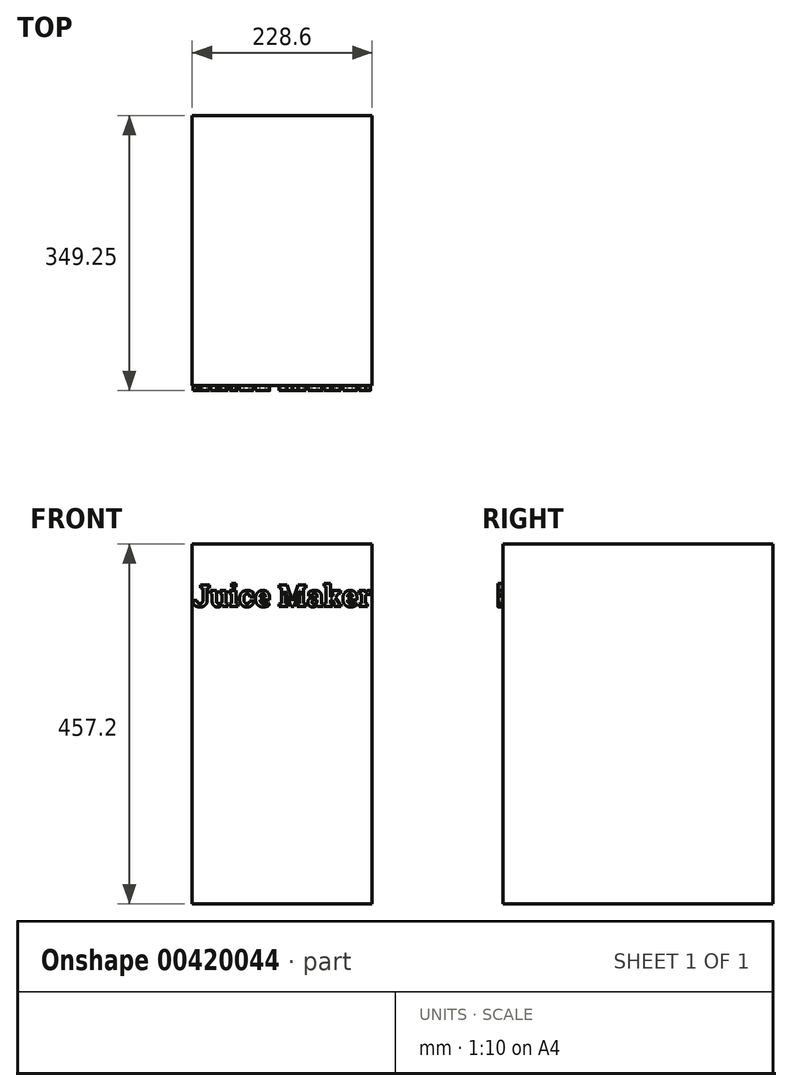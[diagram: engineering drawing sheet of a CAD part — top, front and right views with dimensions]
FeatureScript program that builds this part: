
annotation { "Feature Type Name" : "Feature", "Feature Type Description" : "" }
export const myFeature = defineFeature(function(context is Context, id is Id, definition is map)
    precondition{}
    {
        {
            var Q0;
            Q0=qCreatedBy(makeId("Front.planeOp"),FACE);
            var sketch = newSketch(context, id + "F0", { "sketchPlane" : qUnion([Q0])});
            skLineSegment(sketch, "E0.bottom", {"start": v(0, 0) * mm, "end": v(228.6, 0) * mm});
            skLineSegment(sketch, "E0.top", {"start": v(0, 457.2) * mm, "end": v(228.6, 457.2) * mm});
            skLineSegment(sketch, "E0.left", {"start": v(0, 0) * mm, "end": v(0, 457.2) * mm});
            skLineSegment(sketch, "E0.right", {"start": v(228.6, 0) * mm, "end": v(228.6, 457.2) * mm});
            skSolve(sketch);
        }
        {
            var Q0;
            Q0=makeQuery(id+"F0.imprint","IMPRINT",FACE,{"disambiguationData":[TD([[makeQuery(id+"F0.imprint","IMPRINT",EDGE,{"derivedFrom":sQuery(id+"F0.wireOp",EDGE,"E0.bottom")}),1.0]])]});
            extrude(context, id + "F1", {"entities" : qUnion([Q0]), "depth" : 342.9 * mm});
        }
        {
            var Q0;
            Q0=makeQuery(id+"F1.opExtrude","CAP_FACE",FACE,{"disambiguationData":[OSD([sQuery(id+"F0.wireOp",EDGE,"E0.bottom"),sQuery(id+"F0.wireOp",EDGE,"E0.top"),sQuery(id+"F0.wireOp",EDGE,"E0.left"),sQuery(id+"F0.wireOp",EDGE,"E0.right")])],"isStart":false});
            var sketch = newSketch(context, id + "F2", { "sketchPlane" : qUnion([Q0])});
            skText(sketch, "E1", { "text": "Juice Maker", "fontName": "RobotoSlab-Bold.ttf"});
            const initialGuessF2  = {"E1": [0, 0.3776, 1, 0, 0.02772]};
            skSetInitialGuess(sketch, initialGuessF2);
            skSolve(sketch);
        }
        {
            var Q0;
            Q0 = qSketchRegion(id + "F2", true);
            extrude(context, id + "F3", {"entities" : qUnion([Q0]), "operationType" : NewBodyOperationType.ADD, "depth" : 6.35 * mm});
        }
    });
